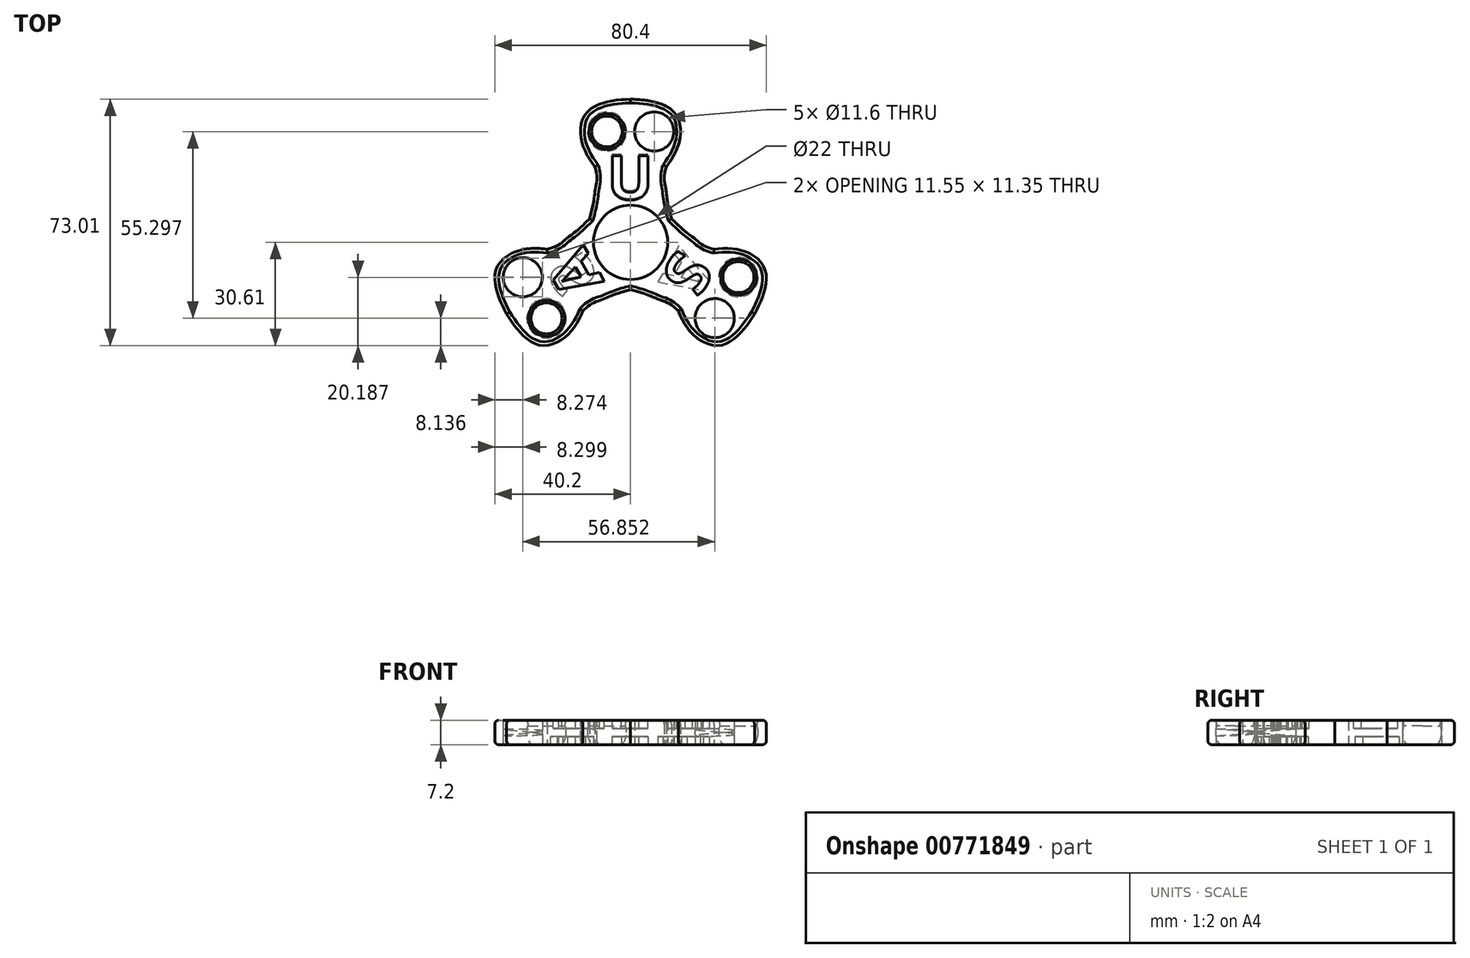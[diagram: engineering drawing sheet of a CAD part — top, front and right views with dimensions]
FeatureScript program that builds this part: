
annotation { "Feature Type Name" : "Feature", "Feature Type Description" : "" }
export const myFeature = defineFeature(function(context is Context, id is Id, definition is map)
    precondition{}
    {
        {
            var Q0;
            Q0=qCreatedBy(makeId("Top.planeOp"),FACE);
            var sketch = newSketch(context, id + "F0", { "sketchPlane" : qUnion([Q0])});
            skCircle(sketch, "E0", {"center": v(0, 0) * mm, "radius": 11 * mm});
            skCircle(sketch, "E1", {"center": v(0, 0) * mm, "radius": 14 * mm});
            skLineSegment(sketch, "E2", {"start": v(-60.62, 35) * mm, "end": v(57.4, -33.14) * mm, "construction": true});
            skLineSegment(sketch, "E3.MirrorCS", {"start": v(-60.62, -35) * mm, "end": v(57.4, 33.14) * mm, "construction": true});
            skFitSpline(sketch, "E4", {"points": [v(-12.12, 7) * mm, v(-10.44, 15.95) * mm, v(-10.57, 22.4) * mm], "startDerivative": vector(9.34, 35.35) * mm, "endDerivative": vector(-6.85, 21.82) * mm});
            skLineSegment(sketch, "E5", {"start": v(-61.07, 42.4) * mm, "end": v(58.93, 42.4) * mm, "construction": true});
            skFitSpline(sketch, "E6", {"points": [v(-10.57, 22.4) * mm, v(-14.78, 33.34) * mm, v(0, 42.4) * mm], "startDerivative": vector(-20.82, 27.32) * mm, "endDerivative": vector(68.91, 1.84) * mm});
            skCircle(sketch, "E7", {"center": v(-7, 32.82) * mm, "radius": 5.8 * mm});
            skFitSpline(sketch, "E8.MirrorCS", {"points": [v(10.57, 22.4) * mm, v(14.78, 33.34) * mm, v(0, 42.4) * mm], "startDerivative": vector(20.82, 27.32) * mm, "endDerivative": vector(-68.91, 1.84) * mm});
            skFitSpline(sketch, "E9.MirrorCS", {"points": [v(12.12, 7) * mm, v(10.44, 15.95) * mm, v(10.57, 22.4) * mm], "startDerivative": vector(-9.34, 35.35) * mm, "endDerivative": vector(6.85, 21.82) * mm});
            skCircle(sketch, "E10.MirrorC", {"center": v(7, 32.82) * mm, "radius": 5.8 * mm});
            skFitSpline(sketch, "E11.MirrorCS", {"points": [v(24.68, -2.05) * mm, v(36.26, -3.87) * mm, v(36.72, -21.2) * mm], "startDerivative": vector(34.07, 4.37) * mm, "endDerivative": vector(-32.86, -60.6) * mm});
            skFitSpline(sketch, "E12.MirrorCS", {"points": [v(12.12, 7) * mm, v(19.03, 1.06) * mm, v(24.68, -2.05) * mm], "startDerivative": vector(25.94, -25.77) * mm, "endDerivative": vector(22.32, -4.98) * mm});
            skFitSpline(sketch, "E13.MirrorCS", {"points": [v(14.12, -20.35) * mm, v(21.48, -29.47) * mm, v(36.72, -21.2) * mm], "startDerivative": vector(13.25, -31.7) * mm, "endDerivative": vector(36.05, 58.76) * mm});
            skFitSpline(sketch, "E14.MirrorCS", {"points": [v(0, -14) * mm, v(8.6, -17.01) * mm, v(14.12, -20.35) * mm], "startDerivative": vector(35.29, -9.59) * mm, "endDerivative": vector(15.48, -16.84) * mm});
            skCircle(sketch, "E15.MirrorC", {"center": v(24.93, -22.47) * mm, "radius": 5.8 * mm});
            skCircle(sketch, "E16.MirrorC", {"center": v(31.93, -10.35) * mm, "radius": 5.8 * mm});
            skFitSpline(sketch, "E17.MirrorCS", {"points": [v(-12.12, 7) * mm, v(-19.03, 1.06) * mm, v(-24.68, -2.05) * mm], "startDerivative": vector(-25.94, -25.77) * mm, "endDerivative": vector(-22.32, -4.98) * mm});
            skFitSpline(sketch, "E18.MirrorCS", {"points": [v(0, -14) * mm, v(-8.6, -17.01) * mm, v(-14.12, -20.35) * mm], "startDerivative": vector(-35.29, -9.59) * mm, "endDerivative": vector(-15.48, -16.84) * mm});
            skFitSpline(sketch, "E19.MirrorCS", {"points": [v(-14.12, -20.35) * mm, v(-21.48, -29.47) * mm, v(-36.72, -21.2) * mm], "startDerivative": vector(-13.25, -31.7) * mm, "endDerivative": vector(-36.05, 58.76) * mm});
            skFitSpline(sketch, "E20.MirrorCS", {"points": [v(-24.68, -2.05) * mm, v(-36.26, -3.87) * mm, v(-36.72, -21.2) * mm], "startDerivative": vector(-34.07, 4.37) * mm, "endDerivative": vector(32.86, -60.6) * mm});
            skCircle(sketch, "E21.MirrorC", {"center": v(-31.93, -10.35) * mm, "radius": 5.8 * mm});
            skCircle(sketch, "E22.MirrorC", {"center": v(-24.93, -22.47) * mm, "radius": 5.8 * mm});
            skSolve(sketch);
        }
        {
            var Q0;
            {var subQ0=sQuery(id+"F0.wireOp",EDGE,"E4");Q0=makeQuery(id+"F0.imprint","IMPRINT",FACE,{"disambiguationData":[TD([[makeQuery(id+"F0.imprint","IMPRINT",EDGE,{"derivedFrom":subQ0}),-1.0]])]});}
            var Q1;
            Q1=makeQuery(id+"F0.imprint","IMPRINT",FACE,{"disambiguationData":[TD([[makeQuery(id+"F0.imprint","IMPRINT",EDGE,{"derivedFrom":sQuery(id+"F0.wireOp",EDGE,"E7")}),1.0]])]});
            var Q2;
            Q2=makeQuery(id+"F0.imprint","IMPRINT",FACE,{"disambiguationData":[TD([[makeQuery(id+"F0.imprint","IMPRINT",EDGE,{"derivedFrom":sQuery(id+"F0.wireOp",EDGE,"E10.MirrorC")}),-1.0]])]});
            var Q3;
            {var subQ0=sQuery(id+"F0.wireOp",EDGE,"E17.MirrorCS");Q3=makeQuery(id+"F0.imprint","IMPRINT",FACE,{"disambiguationData":[TD([[makeQuery(id+"F0.imprint","IMPRINT",EDGE,{"derivedFrom":subQ0}),1.0]])]});}
            var Q4;
            Q4=makeQuery(id+"F0.imprint","IMPRINT",FACE,{"disambiguationData":[TD([[makeQuery(id+"F0.imprint","IMPRINT",EDGE,{"derivedFrom":sQuery(id+"F0.wireOp",EDGE,"E11.MirrorCS")}),-1.0]])]});
            var Q5;
            Q5=makeQuery(id+"F0.imprint","IMPRINT",FACE,{"disambiguationData":[TD([[makeQuery(id+"F0.imprint","IMPRINT",EDGE,{"derivedFrom":sQuery(id+"F0.wireOp",EDGE,"E0")}),-1.0]])]});
            var Q6;
            Q6=makeQuery(id+"F0.imprint","IMPRINT",FACE,{"disambiguationData":[TD([[makeQuery(id+"F0.imprint","IMPRINT",EDGE,{"derivedFrom":sQuery(id+"F0.wireOp",EDGE,"E22.MirrorC")}),1.0]])]});
            var Q7;
            Q7=makeQuery(id+"F0.imprint","IMPRINT",FACE,{"disambiguationData":[TD([[makeQuery(id+"F0.imprint","IMPRINT",EDGE,{"derivedFrom":sQuery(id+"F0.wireOp",EDGE,"E21.MirrorC")}),-1.0]])]});
            var Q8;
            Q8=makeQuery(id+"F0.imprint","IMPRINT",FACE,{"disambiguationData":[TD([[makeQuery(id+"F0.imprint","IMPRINT",EDGE,{"derivedFrom":sQuery(id+"F0.wireOp",EDGE,"E15.MirrorC")}),-1.0]])]});
            var Q9;
            Q9=makeQuery(id+"F0.imprint","IMPRINT",FACE,{"disambiguationData":[TD([[makeQuery(id+"F0.imprint","IMPRINT",EDGE,{"derivedFrom":sQuery(id+"F0.wireOp",EDGE,"E16.MirrorC")}),1.0]])]});
            extrude(context, id + "F1", {"entities" : qUnion([Q0, Q1, Q2, Q3, Q4, Q5, Q6, Q7, Q8, Q9]), "depth" : 7.2 * mm, "offsetDistance" : 25 * mm});
        }
        {
            var Q0;
            Q0=qCreatedBy(makeId("Top.planeOp"),FACE);
            cPlane(context, id + "F2", {"entities" : qUnion([Q0]), "cplaneType" : CPlaneType.OFFSET, "offset" : 3.6 * mm, "width" : 150 * mm, "height" : 150 * mm});
        }
        {
            var Q0;
            Q0=qCreatedBy(id+"F2.planeOp",FACE);
            var sketch = newSketch(context, id + "F3", { "sketchPlane" : qUnion([Q0])});
            skArc(sketch, "E23.0", {"start": v(-1.2, 32.82) * mm, "mid": v(-7, 38.62) * mm, "end": v(-12.8, 32.82) * mm});
            skArc(sketch, "E24.0", {"start": v(1.2, 32.82) * mm, "mid": v(7, 38.62) * mm, "end": v(12.8, 32.82) * mm});
            skLineSegment(sketch, "E25", {"start": v(-12.8, 32.82) * mm, "end": v(-1.2, 32.82) * mm});
            skLineSegment(sketch, "E26.MirrorCS", {"start": v(12.8, 32.82) * mm, "end": v(1.2, 32.82) * mm});
            skSolve(sketch);
        }
        {
            var Q0;
            Q0 = qSketchRegion(id + "F3", true);
            var Q1;
            Q1=sQuery(id+"F3.wireOp",EDGE,"E25");
            revolve(context, id + "F4", {"operationType" : NewBodyOperationType.REMOVE, "surfaceOperationType" : NewSurfaceOperationType.NEW, "entities" : qUnion([Q0]), "axis" : qUnion([Q1]), "revolveType" : RevolveType.FULL, "oppositeDirection" : true});
        }
        {
            var Q0;
            Q0=qCreatedBy(id+"F2.planeOp",FACE);
            var sketch = newSketch(context, id + "F5", { "sketchPlane" : qUnion([Q0])});
            skLineSegment(sketch, "E27.MirrorCS", {"start": v(-34.88, -5.24) * mm, "end": v(-29.03, -15.37) * mm});
            skLineSegment(sketch, "E28.MirrorCS", {"start": v(-21.98, -27.58) * mm, "end": v(-27.83, -17.45) * mm});
            skArc(sketch, "E29.MirrorCS", {"start": v(-27.83, -17.45) * mm, "mid": v(-29.97, -25.44) * mm, "end": v(-21.98, -27.58) * mm});
            skArc(sketch, "E30.MirrorCS", {"start": v(-29.03, -15.37) * mm, "mid": v(-37.02, -13.23) * mm, "end": v(-34.88, -5.24) * mm});
            skSolve(sketch);
        }
        {
            var Q0;
            Q0 = qSketchRegion(id + "F5", true);
            var Q1;
            Q1=sQuery(id+"F5.wireOp",EDGE,"E27.MirrorCS");
            revolve(context, id + "F6", {"operationType" : NewBodyOperationType.REMOVE, "surfaceOperationType" : NewSurfaceOperationType.NEW, "entities" : qUnion([Q0]), "axis" : qUnion([Q1]), "revolveType" : RevolveType.FULL, "oppositeDirection" : true});
        }
        {
            var Q0;
            Q0=qCreatedBy(id+"F2.planeOp",FACE);
            var sketch = newSketch(context, id + "F7", { "sketchPlane" : qUnion([Q0])});
            skLineSegment(sketch, "E31.MirrorCS", {"start": v(34.88, -5.24) * mm, "end": v(29.03, -15.37) * mm});
            skLineSegment(sketch, "E32.MirrorCS", {"start": v(21.98, -27.58) * mm, "end": v(27.83, -17.45) * mm});
            skArc(sketch, "E33.MirrorCS", {"start": v(27.83, -17.45) * mm, "mid": v(29.97, -25.44) * mm, "end": v(21.98, -27.58) * mm});
            skArc(sketch, "E34.MirrorCS", {"start": v(29.03, -15.37) * mm, "mid": v(37.02, -13.23) * mm, "end": v(34.88, -5.24) * mm});
            skSolve(sketch);
        }
        {
            var Q0;
            Q0 = qSketchRegion(id + "F7", true);
            var Q1;
            Q1=sQuery(id+"F7.wireOp",EDGE,"E32.MirrorCS");
            revolve(context, id + "F8", {"operationType" : NewBodyOperationType.REMOVE, "surfaceOperationType" : NewSurfaceOperationType.NEW, "entities" : qUnion([Q0]), "axis" : qUnion([Q1]), "revolveType" : RevolveType.FULL, "oppositeDirection" : true});
        }
        {
            var Q0;
            Q0=makeQuery(id+"F4.boolean.opBoolean","INTERSECT",EDGE,{"derivedFrom":[makeQuery(id+"F1.opExtrude","CAP_FACE",FACE,{"disambiguationData":[OSD([sQuery(id+"F0.wireOp",EDGE,"E0"),sQuery(id+"F0.wireOp",EDGE,"E4"),sQuery(id+"F0.wireOp",EDGE,"E6"),sQuery(id+"F0.wireOp",EDGE,"E8.MirrorCS"),sQuery(id+"F0.wireOp",EDGE,"E9.MirrorCS"),sQuery(id+"F0.wireOp",EDGE,"E11.MirrorCS"),sQuery(id+"F0.wireOp",EDGE,"E12.MirrorCS"),sQuery(id+"F0.wireOp",EDGE,"E13.MirrorCS"),sQuery(id+"F0.wireOp",EDGE,"E14.MirrorCS"),sQuery(id+"F0.wireOp",EDGE,"E17.MirrorCS"),sQuery(id+"F0.wireOp",EDGE,"E18.MirrorCS"),sQuery(id+"F0.wireOp",EDGE,"E19.MirrorCS"),sQuery(id+"F0.wireOp",EDGE,"E20.MirrorCS")])],"isStart":false}),makeQuery(id+"F4.opRevolve","SWEPT_FACE",FACE,{"disambiguationData":[OSD([sQuery(id+"F3.wireOp",EDGE,"E23.0")])]})]});
            var Q1;
            Q1=makeQuery(id+"F4.boolean.opBoolean","INTERSECT",EDGE,{"derivedFrom":[makeQuery(id+"F1.opExtrude","CAP_FACE",FACE,{"disambiguationData":[OSD([sQuery(id+"F0.wireOp",EDGE,"E0"),sQuery(id+"F0.wireOp",EDGE,"E4"),sQuery(id+"F0.wireOp",EDGE,"E6"),sQuery(id+"F0.wireOp",EDGE,"E8.MirrorCS"),sQuery(id+"F0.wireOp",EDGE,"E9.MirrorCS"),sQuery(id+"F0.wireOp",EDGE,"E11.MirrorCS"),sQuery(id+"F0.wireOp",EDGE,"E12.MirrorCS"),sQuery(id+"F0.wireOp",EDGE,"E13.MirrorCS"),sQuery(id+"F0.wireOp",EDGE,"E14.MirrorCS"),sQuery(id+"F0.wireOp",EDGE,"E17.MirrorCS"),sQuery(id+"F0.wireOp",EDGE,"E18.MirrorCS"),sQuery(id+"F0.wireOp",EDGE,"E19.MirrorCS"),sQuery(id+"F0.wireOp",EDGE,"E20.MirrorCS")])],"isStart":false}),makeQuery(id+"F4.opRevolve","SWEPT_FACE",FACE,{"disambiguationData":[OSD([sQuery(id+"F3.wireOp",EDGE,"E24.0")])]})]});
            var Q2;
            Q2=makeQuery(id+"F8.boolean.opBoolean","INTERSECT",EDGE,{"derivedFrom":[makeQuery(id+"F1.opExtrude","CAP_FACE",FACE,{"disambiguationData":[OSD([sQuery(id+"F0.wireOp",EDGE,"E0"),sQuery(id+"F0.wireOp",EDGE,"E4"),sQuery(id+"F0.wireOp",EDGE,"E6"),sQuery(id+"F0.wireOp",EDGE,"E8.MirrorCS"),sQuery(id+"F0.wireOp",EDGE,"E9.MirrorCS"),sQuery(id+"F0.wireOp",EDGE,"E11.MirrorCS"),sQuery(id+"F0.wireOp",EDGE,"E12.MirrorCS"),sQuery(id+"F0.wireOp",EDGE,"E13.MirrorCS"),sQuery(id+"F0.wireOp",EDGE,"E14.MirrorCS"),sQuery(id+"F0.wireOp",EDGE,"E17.MirrorCS"),sQuery(id+"F0.wireOp",EDGE,"E18.MirrorCS"),sQuery(id+"F0.wireOp",EDGE,"E19.MirrorCS"),sQuery(id+"F0.wireOp",EDGE,"E20.MirrorCS")])],"isStart":false}),makeQuery(id+"F8.opRevolve","SWEPT_FACE",FACE,{"disambiguationData":[OSD([sQuery(id+"F7.wireOp",EDGE,"E34.MirrorCS")])]})]});
            var Q3;
            Q3=makeQuery(id+"F8.boolean.opBoolean","INTERSECT",EDGE,{"derivedFrom":[makeQuery(id+"F1.opExtrude","CAP_FACE",FACE,{"disambiguationData":[OSD([sQuery(id+"F0.wireOp",EDGE,"E0"),sQuery(id+"F0.wireOp",EDGE,"E4"),sQuery(id+"F0.wireOp",EDGE,"E6"),sQuery(id+"F0.wireOp",EDGE,"E8.MirrorCS"),sQuery(id+"F0.wireOp",EDGE,"E9.MirrorCS"),sQuery(id+"F0.wireOp",EDGE,"E11.MirrorCS"),sQuery(id+"F0.wireOp",EDGE,"E12.MirrorCS"),sQuery(id+"F0.wireOp",EDGE,"E13.MirrorCS"),sQuery(id+"F0.wireOp",EDGE,"E14.MirrorCS"),sQuery(id+"F0.wireOp",EDGE,"E17.MirrorCS"),sQuery(id+"F0.wireOp",EDGE,"E18.MirrorCS"),sQuery(id+"F0.wireOp",EDGE,"E19.MirrorCS"),sQuery(id+"F0.wireOp",EDGE,"E20.MirrorCS")])],"isStart":false}),makeQuery(id+"F8.opRevolve","SWEPT_FACE",FACE,{"disambiguationData":[OSD([sQuery(id+"F7.wireOp",EDGE,"E33.MirrorCS")])]})]});
            var Q4;
            Q4=makeQuery(id+"F6.boolean.opBoolean","INTERSECT",EDGE,{"derivedFrom":[makeQuery(id+"F1.opExtrude","CAP_FACE",FACE,{"disambiguationData":[OSD([sQuery(id+"F0.wireOp",EDGE,"E0"),sQuery(id+"F0.wireOp",EDGE,"E4"),sQuery(id+"F0.wireOp",EDGE,"E6"),sQuery(id+"F0.wireOp",EDGE,"E8.MirrorCS"),sQuery(id+"F0.wireOp",EDGE,"E9.MirrorCS"),sQuery(id+"F0.wireOp",EDGE,"E11.MirrorCS"),sQuery(id+"F0.wireOp",EDGE,"E12.MirrorCS"),sQuery(id+"F0.wireOp",EDGE,"E13.MirrorCS"),sQuery(id+"F0.wireOp",EDGE,"E14.MirrorCS"),sQuery(id+"F0.wireOp",EDGE,"E17.MirrorCS"),sQuery(id+"F0.wireOp",EDGE,"E18.MirrorCS"),sQuery(id+"F0.wireOp",EDGE,"E19.MirrorCS"),sQuery(id+"F0.wireOp",EDGE,"E20.MirrorCS")])],"isStart":false}),makeQuery(id+"F6.opRevolve","SWEPT_FACE",FACE,{"disambiguationData":[OSD([sQuery(id+"F5.wireOp",EDGE,"E29.MirrorCS")])]})]});
            var Q5;
            Q5=makeQuery(id+"F6.boolean.opBoolean","INTERSECT",EDGE,{"derivedFrom":[makeQuery(id+"F1.opExtrude","CAP_FACE",FACE,{"disambiguationData":[OSD([sQuery(id+"F0.wireOp",EDGE,"E0"),sQuery(id+"F0.wireOp",EDGE,"E4"),sQuery(id+"F0.wireOp",EDGE,"E6"),sQuery(id+"F0.wireOp",EDGE,"E8.MirrorCS"),sQuery(id+"F0.wireOp",EDGE,"E9.MirrorCS"),sQuery(id+"F0.wireOp",EDGE,"E11.MirrorCS"),sQuery(id+"F0.wireOp",EDGE,"E12.MirrorCS"),sQuery(id+"F0.wireOp",EDGE,"E13.MirrorCS"),sQuery(id+"F0.wireOp",EDGE,"E14.MirrorCS"),sQuery(id+"F0.wireOp",EDGE,"E17.MirrorCS"),sQuery(id+"F0.wireOp",EDGE,"E18.MirrorCS"),sQuery(id+"F0.wireOp",EDGE,"E19.MirrorCS"),sQuery(id+"F0.wireOp",EDGE,"E20.MirrorCS")])],"isStart":false}),makeQuery(id+"F6.opRevolve","SWEPT_FACE",FACE,{"disambiguationData":[OSD([sQuery(id+"F5.wireOp",EDGE,"E30.MirrorCS")])]})]});
            fillet(context, id + "F9", {"entities" : qUnion([Q0, Q1, Q2, Q3, Q4, Q5]), "radius" : 1.2 * mm, "tangentPropagation" : true, "allowEdgeOverflow" : false});
        }
        {
            var Q0;
            Q0=makeQuery(id+"F1.opExtrude","CAP_EDGE",EDGE,{"disambiguationData":[OSD([sQuery(id+"F0.wireOp",EDGE,"E6")])],"isStart":false});
            var Q1;
            Q1=makeQuery(id+"F1.opExtrude","CAP_EDGE",EDGE,{"disambiguationData":[OSD([sQuery(id+"F0.wireOp",EDGE,"E4")])],"isStart":false});
            var Q2;
            Q2=makeQuery(id+"F1.opExtrude","CAP_EDGE",EDGE,{"disambiguationData":[OSD([sQuery(id+"F0.wireOp",EDGE,"E8.MirrorCS")])],"isStart":false});
            var Q3;
            Q3=makeQuery(id+"F1.opExtrude","CAP_EDGE",EDGE,{"disambiguationData":[OSD([sQuery(id+"F0.wireOp",EDGE,"E9.MirrorCS")])],"isStart":false});
            var Q4;
            Q4=makeQuery(id+"F1.opExtrude","CAP_EDGE",EDGE,{"disambiguationData":[OSD([sQuery(id+"F0.wireOp",EDGE,"E4")])],"isStart":true});
            var Q5;
            Q5=makeQuery(id+"F1.opExtrude","CAP_EDGE",EDGE,{"disambiguationData":[OSD([sQuery(id+"F0.wireOp",EDGE,"E9.MirrorCS")])],"isStart":true});
            var Q6;
            Q6=makeQuery(id+"F1.opExtrude","CAP_EDGE",EDGE,{"disambiguationData":[OSD([sQuery(id+"F0.wireOp",EDGE,"E8.MirrorCS")])],"isStart":true});
            var Q7;
            Q7=makeQuery(id+"F1.opExtrude","CAP_EDGE",EDGE,{"disambiguationData":[OSD([sQuery(id+"F0.wireOp",EDGE,"E6")])],"isStart":true});
            var Q8;
            Q8=makeQuery(id+"F1.opExtrude","CAP_EDGE",EDGE,{"disambiguationData":[OSD([sQuery(id+"F0.wireOp",EDGE,"E17.MirrorCS")])],"isStart":false});
            var Q9;
            Q9=makeQuery(id+"F1.opExtrude","CAP_EDGE",EDGE,{"disambiguationData":[OSD([sQuery(id+"F0.wireOp",EDGE,"E20.MirrorCS")])],"isStart":false});
            var Q10;
            Q10=makeQuery(id+"F1.opExtrude","CAP_EDGE",EDGE,{"disambiguationData":[OSD([sQuery(id+"F0.wireOp",EDGE,"E19.MirrorCS")])],"isStart":false});
            var Q11;
            Q11=makeQuery(id+"F1.opExtrude","CAP_EDGE",EDGE,{"disambiguationData":[OSD([sQuery(id+"F0.wireOp",EDGE,"E18.MirrorCS")])],"isStart":false});
            var Q12;
            Q12=makeQuery(id+"F1.opExtrude","CAP_EDGE",EDGE,{"disambiguationData":[OSD([sQuery(id+"F0.wireOp",EDGE,"E14.MirrorCS")])],"isStart":false});
            var Q13;
            Q13=makeQuery(id+"F1.opExtrude","CAP_EDGE",EDGE,{"disambiguationData":[OSD([sQuery(id+"F0.wireOp",EDGE,"E13.MirrorCS")])],"isStart":false});
            var Q14;
            Q14=makeQuery(id+"F1.opExtrude","CAP_EDGE",EDGE,{"disambiguationData":[OSD([sQuery(id+"F0.wireOp",EDGE,"E11.MirrorCS")])],"isStart":false});
            var Q15;
            Q15=makeQuery(id+"F1.opExtrude","CAP_EDGE",EDGE,{"disambiguationData":[OSD([sQuery(id+"F0.wireOp",EDGE,"E12.MirrorCS")])],"isStart":false});
            var Q16;
            Q16=makeQuery(id+"F1.opExtrude","CAP_EDGE",EDGE,{"disambiguationData":[OSD([sQuery(id+"F0.wireOp",EDGE,"E12.MirrorCS")])],"isStart":true});
            var Q17;
            Q17=makeQuery(id+"F1.opExtrude","CAP_EDGE",EDGE,{"disambiguationData":[OSD([sQuery(id+"F0.wireOp",EDGE,"E17.MirrorCS")])],"isStart":true});
            var Q18;
            Q18=makeQuery(id+"F1.opExtrude","CAP_EDGE",EDGE,{"disambiguationData":[OSD([sQuery(id+"F0.wireOp",EDGE,"E20.MirrorCS")])],"isStart":true});
            var Q19;
            Q19=makeQuery(id+"F1.opExtrude","CAP_EDGE",EDGE,{"disambiguationData":[OSD([sQuery(id+"F0.wireOp",EDGE,"E19.MirrorCS")])],"isStart":true});
            var Q20;
            Q20=makeQuery(id+"F1.opExtrude","CAP_EDGE",EDGE,{"disambiguationData":[OSD([sQuery(id+"F0.wireOp",EDGE,"E18.MirrorCS")])],"isStart":true});
            var Q21;
            Q21=makeQuery(id+"F1.opExtrude","CAP_EDGE",EDGE,{"disambiguationData":[OSD([sQuery(id+"F0.wireOp",EDGE,"E14.MirrorCS")])],"isStart":true});
            var Q22;
            Q22=makeQuery(id+"F1.opExtrude","CAP_EDGE",EDGE,{"disambiguationData":[OSD([sQuery(id+"F0.wireOp",EDGE,"E13.MirrorCS")])],"isStart":true});
            var Q23;
            Q23=makeQuery(id+"F1.opExtrude","CAP_EDGE",EDGE,{"disambiguationData":[OSD([sQuery(id+"F0.wireOp",EDGE,"E11.MirrorCS")])],"isStart":true});
            fillet(context, id + "F10", {"entities" : qUnion([Q0, Q1, Q2, Q3, Q4, Q5, Q6, Q7, Q8, Q9, Q10, Q11, Q12, Q13, Q14, Q15, Q16, Q17, Q18, Q19, Q20, Q21, Q22, Q23]), "radius" : 1.1 * mm, "tangentPropagation" : true, "allowEdgeOverflow" : false});
        }
        {
            var Q0;
            Q0=makeQuery(id+"F1.opExtrude","CAP_FACE",FACE,{"disambiguationData":[OSD([sQuery(id+"F0.wireOp",EDGE,"E0"),sQuery(id+"F0.wireOp",EDGE,"E4"),sQuery(id+"F0.wireOp",EDGE,"E6"),sQuery(id+"F0.wireOp",EDGE,"E8.MirrorCS"),sQuery(id+"F0.wireOp",EDGE,"E9.MirrorCS"),sQuery(id+"F0.wireOp",EDGE,"E11.MirrorCS"),sQuery(id+"F0.wireOp",EDGE,"E12.MirrorCS"),sQuery(id+"F0.wireOp",EDGE,"E13.MirrorCS"),sQuery(id+"F0.wireOp",EDGE,"E14.MirrorCS"),sQuery(id+"F0.wireOp",EDGE,"E17.MirrorCS"),sQuery(id+"F0.wireOp",EDGE,"E18.MirrorCS"),sQuery(id+"F0.wireOp",EDGE,"E19.MirrorCS"),sQuery(id+"F0.wireOp",EDGE,"E20.MirrorCS")])],"isStart":false});
            var sketch = newSketch(context, id + "F11", { "sketchPlane" : qUnion([Q0])});
            skText(sketch, "E35", { "text": "U", "fontName": "NotoSans-Bold.ttf"});
            skText(sketch, "E36", { "text": "S", "fontName": "NotoSans-Bold.ttf"});
            skText(sketch, "E37", { "text": "A", "fontName": "NotoSans-Bold.ttf"});
            const initialGuessF11  = {"E35": [-0.00696, 0.0127, 1, 0, 0.013], "E36": [0.01387, -0.0017, -0.5, -0.86603, 0.013], "E37": [-0.00776, -0.0115, -0.5, 0.86603, 0.013]};
            skSetInitialGuess(sketch, initialGuessF11);
            skSolve(sketch);
        }
        {
            var Q0;
            Q0=makeQuery(id+"F1.opExtrude","CAP_FACE",FACE,{"disambiguationData":[OSD([sQuery(id+"F0.wireOp",EDGE,"E0"),sQuery(id+"F0.wireOp",EDGE,"E4"),sQuery(id+"F0.wireOp",EDGE,"E6"),sQuery(id+"F0.wireOp",EDGE,"E8.MirrorCS"),sQuery(id+"F0.wireOp",EDGE,"E9.MirrorCS"),sQuery(id+"F0.wireOp",EDGE,"E11.MirrorCS"),sQuery(id+"F0.wireOp",EDGE,"E12.MirrorCS"),sQuery(id+"F0.wireOp",EDGE,"E13.MirrorCS"),sQuery(id+"F0.wireOp",EDGE,"E14.MirrorCS"),sQuery(id+"F0.wireOp",EDGE,"E17.MirrorCS"),sQuery(id+"F0.wireOp",EDGE,"E18.MirrorCS"),sQuery(id+"F0.wireOp",EDGE,"E19.MirrorCS"),sQuery(id+"F0.wireOp",EDGE,"E20.MirrorCS")])],"isStart":true});
            var sketch = newSketch(context, id + "F12", { "sketchPlane" : qUnion([Q0])});
            skText(sketch, "E38", { "text": "U", "fontName": "NotoSans-Bold.ttf"});
            skText(sketch, "E39", { "text": "S", "fontName": "NotoSans-Bold.ttf"});
            skText(sketch, "E40", { "text": "A", "fontName": "NotoSans-Bold.ttf"});
            const initialGuessF12  = {"E38": [0.00665, -0.0131, -1, 0, 0.013], "E39": [-0.01417, 0.00204, 0.5, 0.86603, 0.013], "E40": [0.0081, 0.01175, 0.5, -0.86603, 0.013]};
            skSetInitialGuess(sketch, initialGuessF12);
            skSolve(sketch);
        }
        {
            var Q0;
            Q0=makeQuery(id+"F11.imprint","IMPRINT",FACE,{"disambiguationData":[TD([[makeQuery(id+"F11.imprint","IMPRINT",EDGE,{"derivedFrom":sQuery(id+"F11.wireOp",EDGE,"E35.sketch_text.stroke-0")}),-1.0]])]});
            var Q1;
            Q1=makeQuery(id+"F11.imprint","IMPRINT",FACE,{"disambiguationData":[TD([[makeQuery(id+"F11.imprint","IMPRINT",EDGE,{"derivedFrom":sQuery(id+"F11.wireOp",EDGE,"E36.sketch_text.stroke-0")}),-1.0]])]});
            var Q2;
            Q2=makeQuery(id+"F11.imprint","IMPRINT",FACE,{"disambiguationData":[TD([[makeQuery(id+"F11.imprint","IMPRINT",EDGE,{"derivedFrom":sQuery(id+"F11.wireOp",EDGE,"E37.sketch_text.stroke-0")}),-1.0]])]});
            extrude(context, id + "F13", {"entities" : qUnion([Q0, Q1, Q2]), "operationType" : NewBodyOperationType.REMOVE, "oppositeDirection" : true, "depth" : 2.4 * mm, "offsetDistance" : 25 * mm});
        }
        {
            var Q0;
            Q0=makeQuery(id+"F12.imprint","IMPRINT",FACE,{"disambiguationData":[TD([[makeQuery(id+"F12.imprint","IMPRINT",EDGE,{"derivedFrom":sQuery(id+"F12.wireOp",EDGE,"E39.sketch_text.stroke-0")}),-1.0]])]});
            var Q1;
            Q1=makeQuery(id+"F12.imprint","IMPRINT",FACE,{"disambiguationData":[TD([[makeQuery(id+"F12.imprint","IMPRINT",EDGE,{"derivedFrom":sQuery(id+"F12.wireOp",EDGE,"E40.sketch_text.stroke-0")}),-1.0]])]});
            var Q2;
            Q2=makeQuery(id+"F12.imprint","IMPRINT",FACE,{"disambiguationData":[TD([[makeQuery(id+"F12.imprint","IMPRINT",EDGE,{"derivedFrom":sQuery(id+"F12.wireOp",EDGE,"E38.sketch_text.stroke-0")}),-1.0]])]});
            extrude(context, id + "F14", {"entities" : qUnion([Q0, Q1, Q2]), "operationType" : NewBodyOperationType.REMOVE, "oppositeDirection" : true, "depth" : 2.4 * mm, "offsetDistance" : 25 * mm});
        }
    });
